# Revit family: Street X1 180LPW
name_source: partatom
category: Осветительные приборы
revit_build: Autodesk Revit 2017 (Build: 20160225_1515(x64)
units: mm (PartAtom-declared; Revit-internal decimal feet)

## family parameters
Всегда вертикально = Да
Источник света = Да
На основе рабочей плоскости = Нет
Общий = Нет
При загрузке вырезать с полостями = Нет
Размер круглого соединителя = Использовать диаметр
Тип детали = Нормальный
Точка расчета площади = Нет

## types (14) — shared parameters
Видимая форма излучения при визуализации = Нет
Изготовитель = LEDEL
Излучение по длине прямоугольника = 362 мм
Излучение по ширине прямоугольника = 173 мм
Классификация нагрузок = Освещение
Комментарии к типоразмеру = Уличные
Светофильтр = 16777215
Смещение цветовой температуры при затухании лампы = <Нет>
Угол наклона = 90.00°

## per-type parameters (varying)
| type | Артикул | Полная установленная мощность | Файл фотометрической сетки |
| Street X1-27-Ш8М-4.0К-05 | X1052 | 27 В·А | Street X1-27-LLI8M-4.0K-05.ies |
| Street X1-115-Ш8М-4.0К-05 | X1029 | 115 В·А | Street X1-115-LLI8M-4.0K-05.ies |
| Street X1-84-Ш8М-4.0К-05 | X1152 | 84 В·А | Street X1-84-LLI8M-4.0K-05.ies |
| Street X1-68-Ш8М-4.0К-05 | X1131 | 68 В·А | Street X1-68-LLI8M-4.0K-05.ies |
| Street X1-53-Ш8М-4.0К-05 | X1101 | 53 В·А | Street X1-53-LLI8M-4.0K-05.ies |
| Street X1-43-Ш8М-4.0К-05 | X1085 | 43 В·А | Street X1-43-LLI8M-4.0K-05.ies |
| Street X1-100-Ш8М-4.0К-05 | X1009 | 100 В·А | Street X1-100-LLI8M-4.0K-05.ies |
| Street X1-27-Ш8М-5.0К-05 | X1046 | 27 В·А | Street X1-27-LLI8M-4.0K-05.ies |
| Street X1-43-Ш8М-5.0К-05 | X1081 | 43 В·А | Street X1-43-LLI8M-4.0K-05.ies |
| Street X1-53-Ш8М-5.0К-05 | X1097 | 53 В·А | Street X1-53-LLI8M-4.0K-05.ies |
| Street X1-68-Ш8М-5.0К-05 | X1123 | 68 В·А | Street X1-68-LLI8M-4.0K-05.ies |
| Street X1-84-Ш8М-5.0К-05 | X1148 | 84 В·А | Street X1-84-LLI8M-4.0K-05.ies |
| Street X1-100-Ш8М-5.0К-05 | X1007 | 100 В·А | Street X1-100-LLI8M-4.0K-05.ies |
| Street X1-115-Ш8М-5.0К-05 | X1027 | 115 В·А | Street X1-115-LLI8M-4.0K-05.ies |
